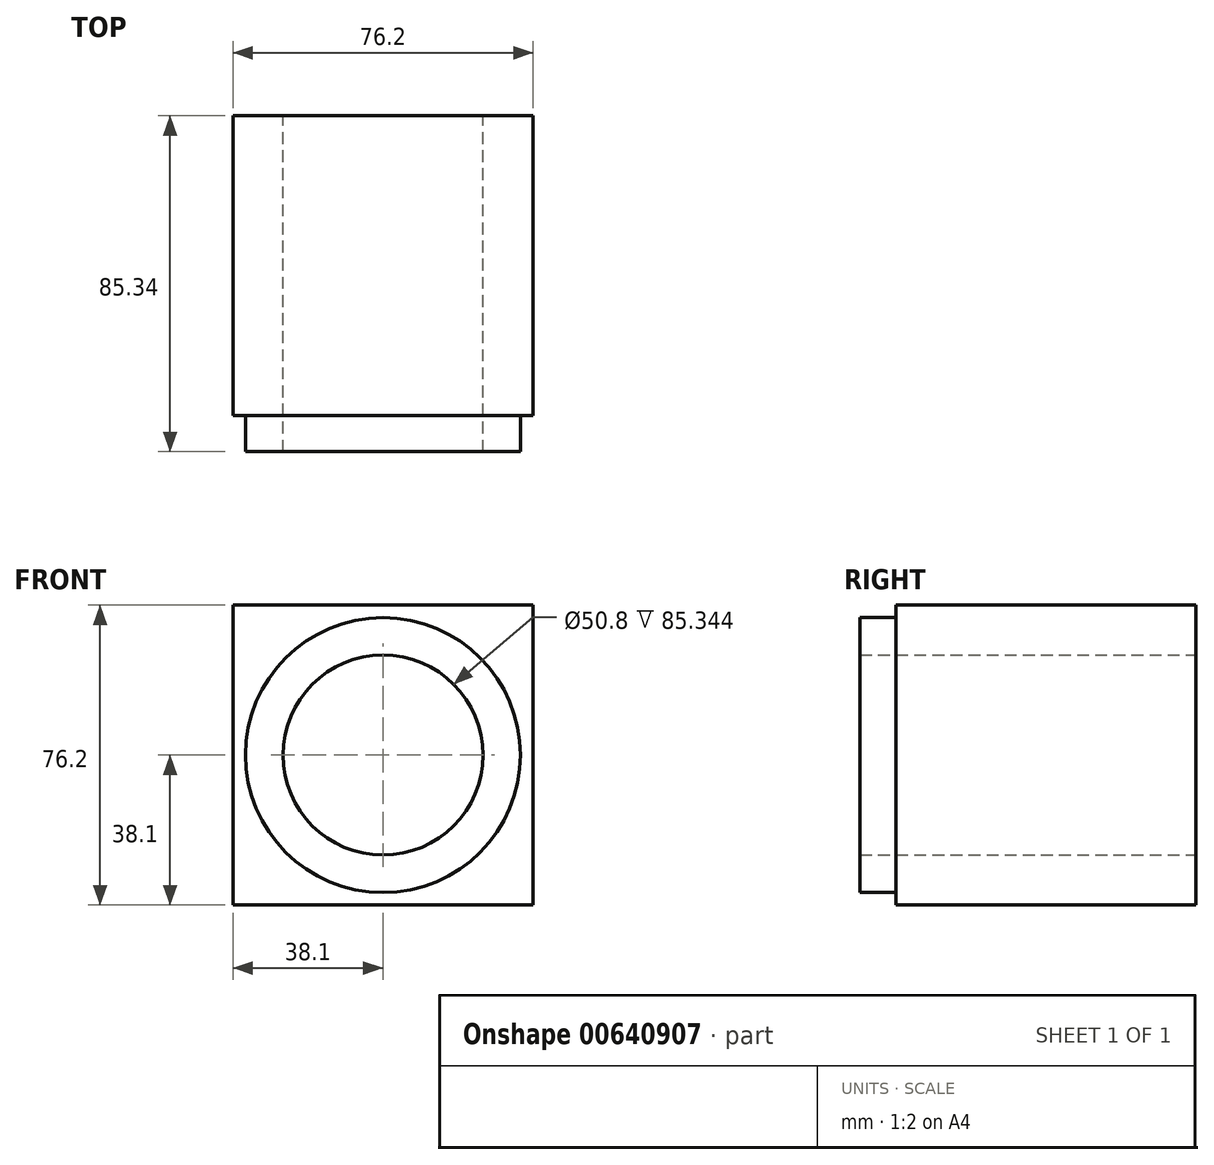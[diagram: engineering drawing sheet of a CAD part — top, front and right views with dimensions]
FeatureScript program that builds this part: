
annotation { "Feature Type Name" : "Feature", "Feature Type Description" : "" }
export const myFeature = defineFeature(function(context is Context, id is Id, definition is map)
    precondition{}
    {
        {
            var Q0;
            Q0=qCreatedBy(makeId("Front.planeOp"),FACE);
            var sketch = newSketch(context, id + "F0", { "sketchPlane" : qUnion([Q0])});
            skLineSegment(sketch, "E0", {"start": v(0, 38.1) * mm, "end": v(38.1, 38.1) * mm});
            skLineSegment(sketch, "E1", {"start": v(38.1, 38.1) * mm, "end": v(38.1, -38.1) * mm});
            skLineSegment(sketch, "E2", {"start": v(38.1, -38.1) * mm, "end": v(-38.1, -38.1) * mm});
            skLineSegment(sketch, "E3", {"start": v(-38.1, -38.1) * mm, "end": v(-38.1, 38.1) * mm});
            skLineSegment(sketch, "E4", {"start": v(-38.1, 38.1) * mm, "end": v(0, 38.1) * mm});
            skCircle(sketch, "E5", {"center": v(0, 0) * mm, "radius": 25.4 * mm});
            skCircle(sketch, "E6", {"center": v(0, 0) * mm, "radius": 34.93 * mm});
            skSolve(sketch);
        }
        {
            var Q0;
            Q0=makeQuery(id+"F0.imprint","IMPRINT",FACE,{"disambiguationData":[TD([[makeQuery(id+"F0.imprint","IMPRINT",EDGE,{"derivedFrom":sQuery(id+"F0.wireOp",EDGE,"E5")}),-1.0]])]});
            extrude(context, id + "F1", {"entities" : qUnion([Q0]), "depth" : 85.34 * mm, "offsetDistance" : 25.4 * mm});
        }
        {
            var Q0;
            Q0 = qSketchRegion(id + "F0", true);
            extrude(context, id + "F2", {"entities" : qUnion([Q0]), "operationType" : NewBodyOperationType.ADD, "depth" : 76.2 * mm, "offsetDistance" : 25.4 * mm});
        }
    });
